# Revit family: 71_98_0503+0513_NESTED
name_source: partatom
category: Communication Devices
revit_build: Autodesk Revit 2015 (Build: 20141119_1515(x64)
units: mm (PartAtom-declared; Revit-internal decimal feet)

## types (6) — shared parameters
Basisplaat = Basisplaat
Breedte = 80 mm  [stored 0.262467 ft]
Default Elevation = 1219 mm
Diepte = 70 mm  [stored 0.229659 ft]
Frequency response = 200-20,000 Hz
Jack = Jack
Kabel = Kabel
Knoppen = Basisplaat
Lengte = 210 mm
Load impedance = 8 Ω
Manufacturer = Televic Conference
Maximum output power = > 1 W
Onderplaat = Inox
Scherm = Jack
Schroef = Basisplaat
Speaker = Jack
THD @ nominal level = < 0.1%
URL = http://www.televic-conference.com
Voltage = 48 V
Weight = 740

## per-type parameters (varying)
| type | Consumption | Dynamic range | Flexible microphone - 71.03.3540 | Microphone - 71.03.3140 | Model | Product ID | Type 71.98.0513 | Type Comments |
| Type 71.98.0503 - flexible microphone | 2 W | > 90 dB | Yes | No | Confidea F-DI | 71.98.0503 | No | Confidea Flushmount Delegate Interpretation Unit |
| Type 71.98.0503 - microphone | 4 W | > 90 dB | No | Yes | Confidea F-DI | 71.98.0503 | No | Confidea Flushmount Delegate Interpretation Unit |
| Type 71.98.0503 - no microphone | 2 W | > 90 dB | No | No | Confidea F-DI | 71.98.0503 | No | Confidea Flushmount Delegate Interpretation Unit |
| Type 71.98.0513 - flexible microphone | 4 W | > 90 dB | Yes | No | Confidea F-CI | 71.98.0513 | Yes | Confidea Flushmount Chairman Interpretation Unit |
| Type 71.98.0513 - microphone | 4 W | > 90 bD | No | Yes | Confidea F-CI | 71.98.0513 | Yes | Confidea Flushmount Chairman Interpretation Unit |
| Type 71.98.0513 - no microphone | 4 W | > 90 dB | No | No | Confidea F-CI | 71.98.0513 | Yes | Confidea Flushmount Chairman Interpretation Unit |

note: [stored X ft] marks values corroborated as IEEE doubles in the binary element streams (Revit-internal decimal feet)

## geometry (parser evidence)
native form markers: Sweep x11
no freeform markers — native parametric forms only
